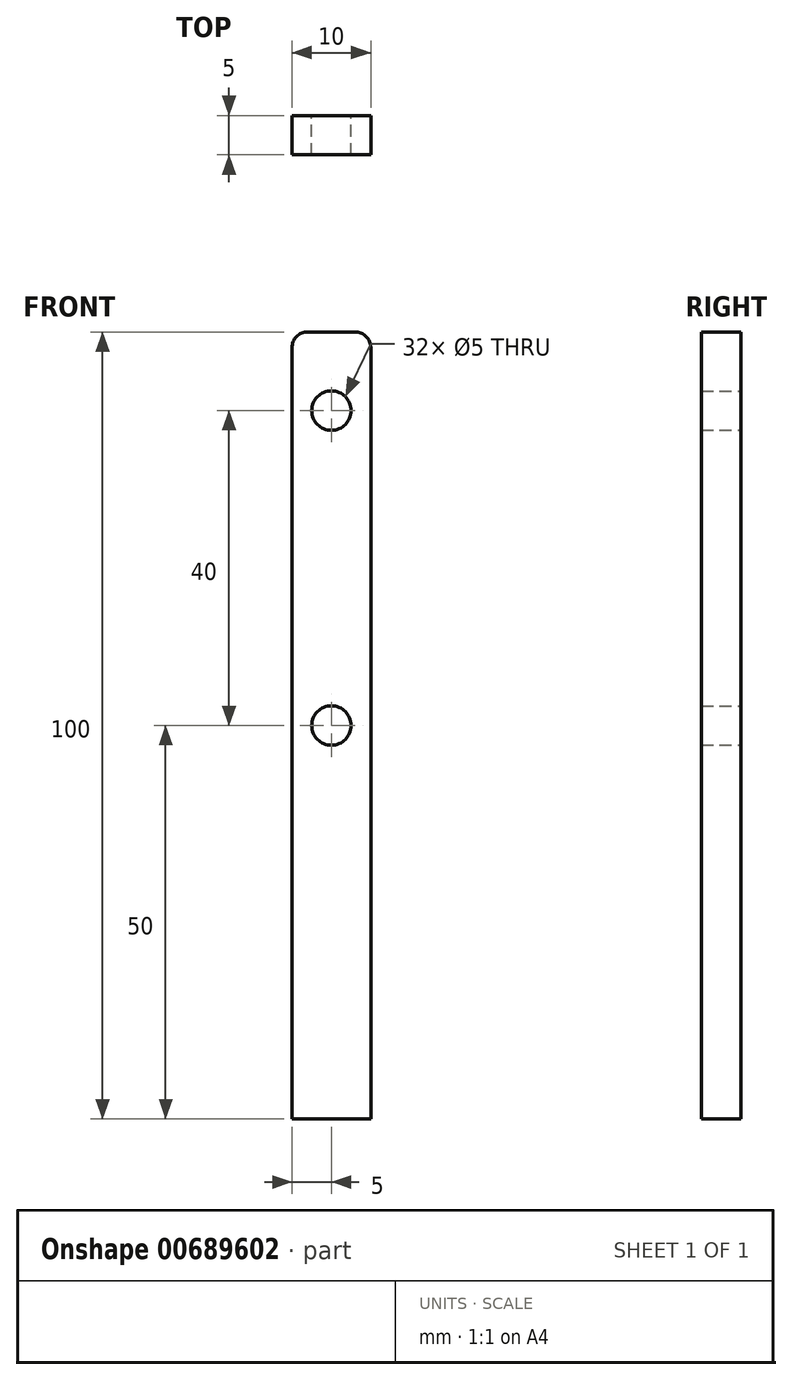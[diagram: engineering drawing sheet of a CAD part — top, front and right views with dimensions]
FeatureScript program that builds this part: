
annotation { "Feature Type Name" : "Feature", "Feature Type Description" : "" }
export const myFeature = defineFeature(function(context is Context, id is Id, definition is map)
    precondition{}
    {
        {
            var Q0;
            Q0=qCreatedBy(makeId("Front.planeOp"),FACE);
            var sketch = newSketch(context, id + "F0", { "sketchPlane" : qUnion([Q0])});
            skLineSegment(sketch, "E0", {"start": v(0, 0) * mm, "end": v(0, 98) * mm});
            skLineSegment(sketch, "E1", {"start": v(2, 100) * mm, "end": v(8, 100) * mm});
            skLineSegment(sketch, "E2", {"start": v(10, 98) * mm, "end": v(10, 0) * mm});
            skLineSegment(sketch, "E3", {"start": v(10, 0) * mm, "end": v(0, 0) * mm});
            skCircle(sketch, "E4", {"center": v(5, 50) * mm, "radius": 2.5 * mm});
            skPoint(sketch, "E5.orphan", {"position": v(10, 50) * mm});
            skPoint(sketch, "E6.orphan", {"position": v(0, 50) * mm});
            skLineSegment(sketch, "E7", {"start": v(10, 50) * mm, "end": v(10, 90) * mm});
            skCircle(sketch, "E8", {"center": v(5, 90) * mm, "radius": 2.5 * mm});
            skPoint(sketch, "E9.first.point", {"position": v(2.74, 100) * mm});
            skPoint(sketch, "E9.second.point", {"position": v(1.45, 96.1) * mm});
            skPoint(sketch, "E9.third.point", {"position": v(0, 97.68) * mm});
            skPoint(sketch, "E10.visualSharp", {"position": v(10, 100) * mm});
            skArc(sketch, "E10.filletArc", {"start": v(10, 98) * mm, "mid": v(9.41, 99.41) * mm, "end": v(8, 100) * mm});
            skPoint(sketch, "E11.visualSharp", {"position": v(0, 100) * mm});
            skArc(sketch, "E11.filletArc", {"start": v(2, 100) * mm, "mid": v(0.59, 99.41) * mm, "end": v(0, 98) * mm});
            skSolve(sketch);
        }
        {
            var Q0;
            Q0=makeQuery(id+"F0.imprint","IMPRINT",FACE,{"disambiguationData":[TD([[makeQuery(id+"F0.imprint","IMPRINT",EDGE,{"derivedFrom":sQuery(id+"F0.wireOp",EDGE,"E0")}),-1.0]])]});
            extrude(context, id + "F1", {"entities" : qUnion([Q0]), "depth" : 5 * mm, "offsetDistance" : 25 * mm});
        }
    });
